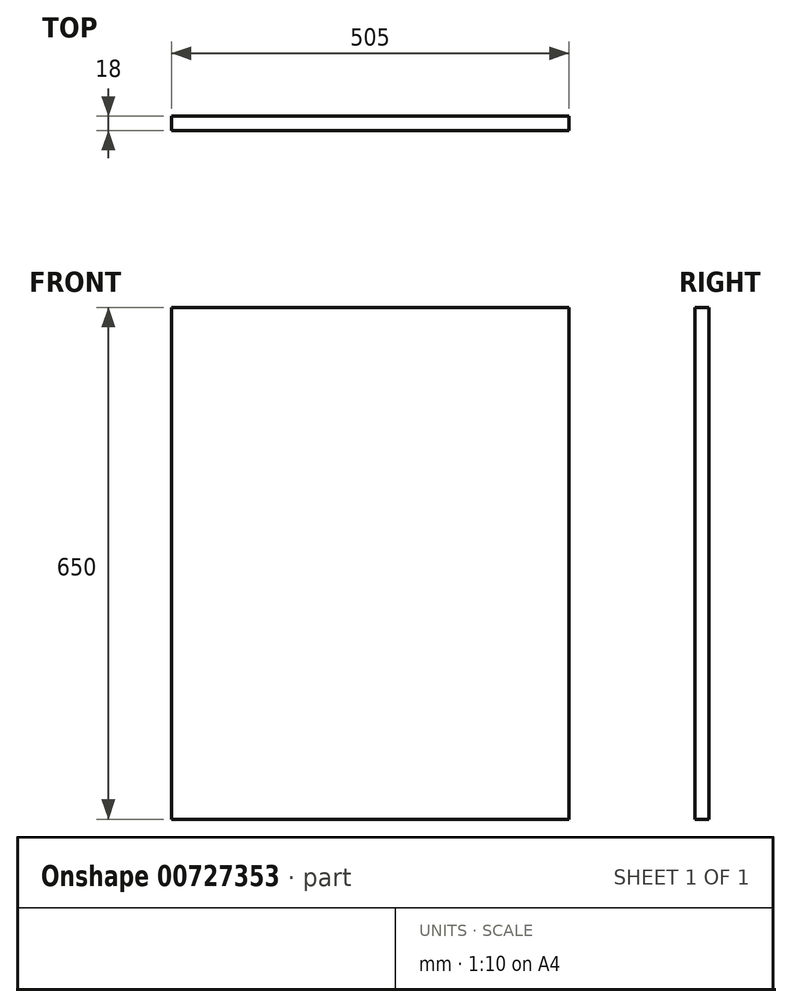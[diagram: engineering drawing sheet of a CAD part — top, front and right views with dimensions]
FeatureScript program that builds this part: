
annotation { "Feature Type Name" : "Feature", "Feature Type Description" : "" }
export const myFeature = defineFeature(function(context is Context, id is Id, definition is map)
    precondition{}
    {
        {
            var Q0;
            Q0=qCreatedBy(makeId("Front.planeOp"),FACE);
            var sketch = newSketch(context, id + "F0", { "sketchPlane" : qUnion([Q0])});
            skLineSegment(sketch, "E0.bottom", {"start": v(0, 0) * mm, "end": v(505, 0) * mm});
            skLineSegment(sketch, "E0.top", {"start": v(0, 650) * mm, "end": v(505, 650) * mm});
            skLineSegment(sketch, "E0.left", {"start": v(0, 0) * mm, "end": v(0, 650) * mm});
            skLineSegment(sketch, "E0.right", {"start": v(505, 0) * mm, "end": v(505, 650) * mm});
            skSolve(sketch);
        }
        {
            var Q0;
            Q0=qSketchRegion(id+"F0",true);
            extrude(context, id + "F1", {"entities" : qUnion([Q0]), "depth" : 18 * mm, "offsetDistance" : 25 * mm});
        }
    });
